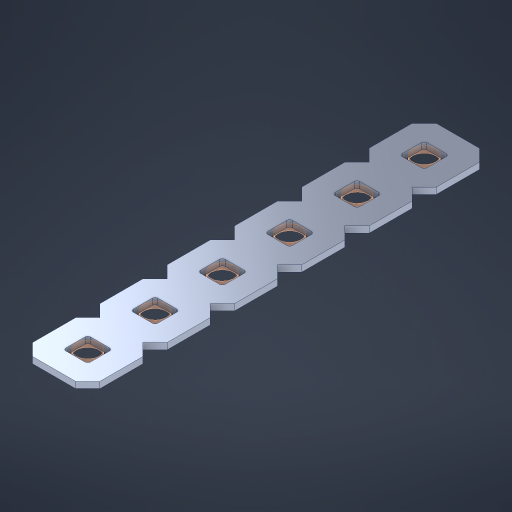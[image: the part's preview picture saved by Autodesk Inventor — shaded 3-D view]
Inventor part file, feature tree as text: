
AUTODESK INVENTOR PART (.ipt)
format: ipt  version: 2023 (Build 270158000, 158)  size: 337,408 bytes
history: native  units: in
note: dims shown in document units (in); Inventor stores cm internally (conversion verified against a paired STEP export)
features: other x7, extrude x5, sketch x2, pattern_linear x1
ambient origin geometry x8: Origin, YZ Plane, XZ Plane, XY Plane, X Axis, Y Axis, Z Axis, Center Point
bodies: Solid1 (feature_tree), Body (feature_tree)
feature tree (15):
  pattern_linear  "Rectangular Pattern1"  Spacing1=0.09in  [1 undecoded]
  sketch  "Sketch1"  dims[d1=0.5in]
  sketch  "Sketch2"  dims[d2=0.182in d3=0.09in d4=0.09in d5=0.09in d6=0.09in d7=0.09in d8=0.09in d9=0.09in d10=0.09in d11=0.02in d13=0.0in d14=0.172in d15=0.0625in d16=0.0in d19=0.5in d22=0.5in]
  other  "Srf1"
  other  "Srf126"
  other  "Srf127"
  other  "Srf128"
  other  "Srf129"
  other  "Srf130"
  other  "Circle"
  extrude  "ExtrusionSrf126"  Depth=0.09in
  extrude  "ExtrusionSrf127"  Depth=0.09in
  extrude  "ExtrusionSrf128"  Depth=0.09in
  extrude  "ExtrusionSrf129"  Depth=0.09in
  extrude  "ExtrusionSrf130"  Depth=0.09in
note: 1 required parameter value undecoded (feature->parameter linkage not recoverable at this tier; creation-order binding heuristic only, values carry confidence <= 0.55)
